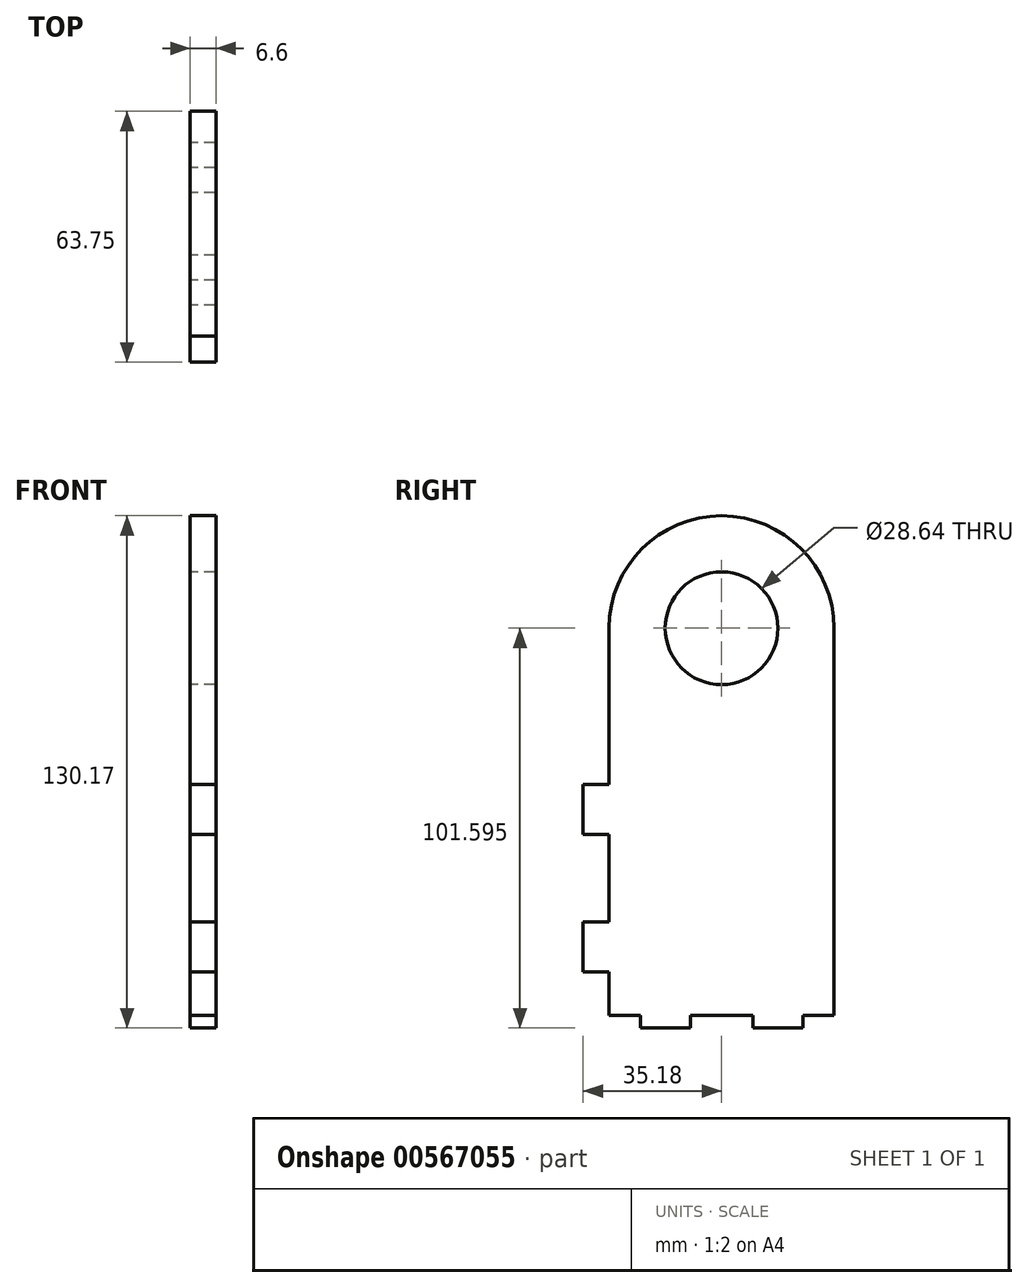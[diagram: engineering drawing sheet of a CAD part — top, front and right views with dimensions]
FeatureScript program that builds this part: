
annotation { "Feature Type Name" : "Feature", "Feature Type Description" : "" }
export const myFeature = defineFeature(function(context is Context, id is Id, definition is map)
    precondition{}
    {
        {
            var Q0;
            Q0=qCreatedBy(makeId("Right.planeOp"),FACE);
            cPlane(context, id + "F0", {"entities" : qUnion([Q0]), "cplaneType" : CPlaneType.OFFSET, "offset" : 101.6 * mm, "width" : 152.4 * mm, "height" : 152.4 * mm});
        }
        {
            var Q0;
            Q0=qCreatedBy(id+"F0.planeOp",FACE);
            var sketch = newSketch(context, id + "F1", { "sketchPlane" : qUnion([Q0])});
            skLineSegment(sketch, "E0.bottom", {"start": v(28.58, 69.85) * mm, "end": v(-28.57, 69.85) * mm});
            skLineSegment(sketch, "E0.top", {"start": v(28.57, 0) * mm, "end": v(-28.58, 0) * mm});
            skLineSegment(sketch, "E0.left", {"start": v(28.57, 69.85) * mm, "end": v(28.57, 0) * mm});
            skLineSegment(sketch, "E0.right", {"start": v(-28.57, 69.85) * mm, "end": v(-28.58, 0) * mm});
            skPoint(sketch, "E0.middle", {"position": v(0, 34.93) * mm});
            skCircle(sketch, "E1", {"center": v(0, 98.43) * mm, "radius": 28.58 * mm});
            skPoint(sketch, "E2", {"position": v(28.58, 98.43) * mm});
            skLineSegment(sketch, "E3", {"start": v(-28.57, 69.85) * mm, "end": v(-28.58, 98.42) * mm});
            skLineSegment(sketch, "E4", {"start": v(28.58, 98.43) * mm, "end": v(28.58, 69.85) * mm});
            skCircle(sketch, "E5", {"center": v(0, 98.43) * mm, "radius": 14.32 * mm});
            skPoint(sketch, "E6.endSnap0", {"position": v(28.57, 34.93) * mm});
            skLineSegment(sketch, "E7", {"start": v(-41.83, 34.93) * mm, "end": v(38.65, 34.93) * mm, "construction": true});
            skPoint(sketch, "E7.endSnap0", {"position": v(-28.58, 34.93) * mm});
            skLineSegment(sketch, "E8.bottom", {"start": v(-28.57, 46.04) * mm, "end": v(-35.18, 46.04) * mm});
            skLineSegment(sketch, "E8.top", {"start": v(-28.57, 58.74) * mm, "end": v(-35.18, 58.74) * mm});
            skLineSegment(sketch, "E8.left", {"start": v(-28.57, 46.04) * mm, "end": v(-28.57, 58.74) * mm});
            skLineSegment(sketch, "E8.right", {"start": v(-35.18, 46.04) * mm, "end": v(-35.18, 58.74) * mm});
            skLineSegment(sketch, "E9.MirrorCS", {"start": v(-28.57, 23.81) * mm, "end": v(-28.57, 11.11) * mm});
            skLineSegment(sketch, "E10.MirrorCS", {"start": v(-35.18, 23.81) * mm, "end": v(-35.18, 11.11) * mm});
            skLineSegment(sketch, "E11.MirrorCS", {"start": v(-28.57, 23.81) * mm, "end": v(-35.18, 23.81) * mm});
            skLineSegment(sketch, "E12.MirrorCS", {"start": v(-28.57, 11.11) * mm, "end": v(-35.18, 11.11) * mm});
            skLineSegment(sketch, "E13.bottom", {"start": v(-20.64, 0) * mm, "end": v(-7.94, 0) * mm});
            skLineSegment(sketch, "E13.top", {"start": v(-20.64, -3.18) * mm, "end": v(-7.94, -3.18) * mm});
            skLineSegment(sketch, "E13.left", {"start": v(-20.64, 0) * mm, "end": v(-20.64, -3.18) * mm});
            skLineSegment(sketch, "E13.right", {"start": v(-7.94, 0) * mm, "end": v(-7.94, -3.18) * mm});
            skLineSegment(sketch, "E14", {"start": v(0, 46.28) * mm, "end": v(0, 23.06) * mm, "construction": true});
            skLineSegment(sketch, "E15.MirrorCS", {"start": v(20.64, -3.18) * mm, "end": v(7.94, -3.18) * mm});
            skLineSegment(sketch, "E16.MirrorCS", {"start": v(7.94, 0) * mm, "end": v(7.94, -3.17) * mm});
            skLineSegment(sketch, "E17.MirrorCS", {"start": v(20.64, 0) * mm, "end": v(7.94, 0) * mm});
            skLineSegment(sketch, "E18.MirrorCS", {"start": v(20.64, 0) * mm, "end": v(20.64, -3.17) * mm});
            skSolve(sketch);
        }
        {
            var Q0;
            Q0=qSketchRegion(id+"F1",true);
            extrude(context, id + "F2", {"entities" : qUnion([Q0]), "depth" : 6.6 * mm});
        }
    });
